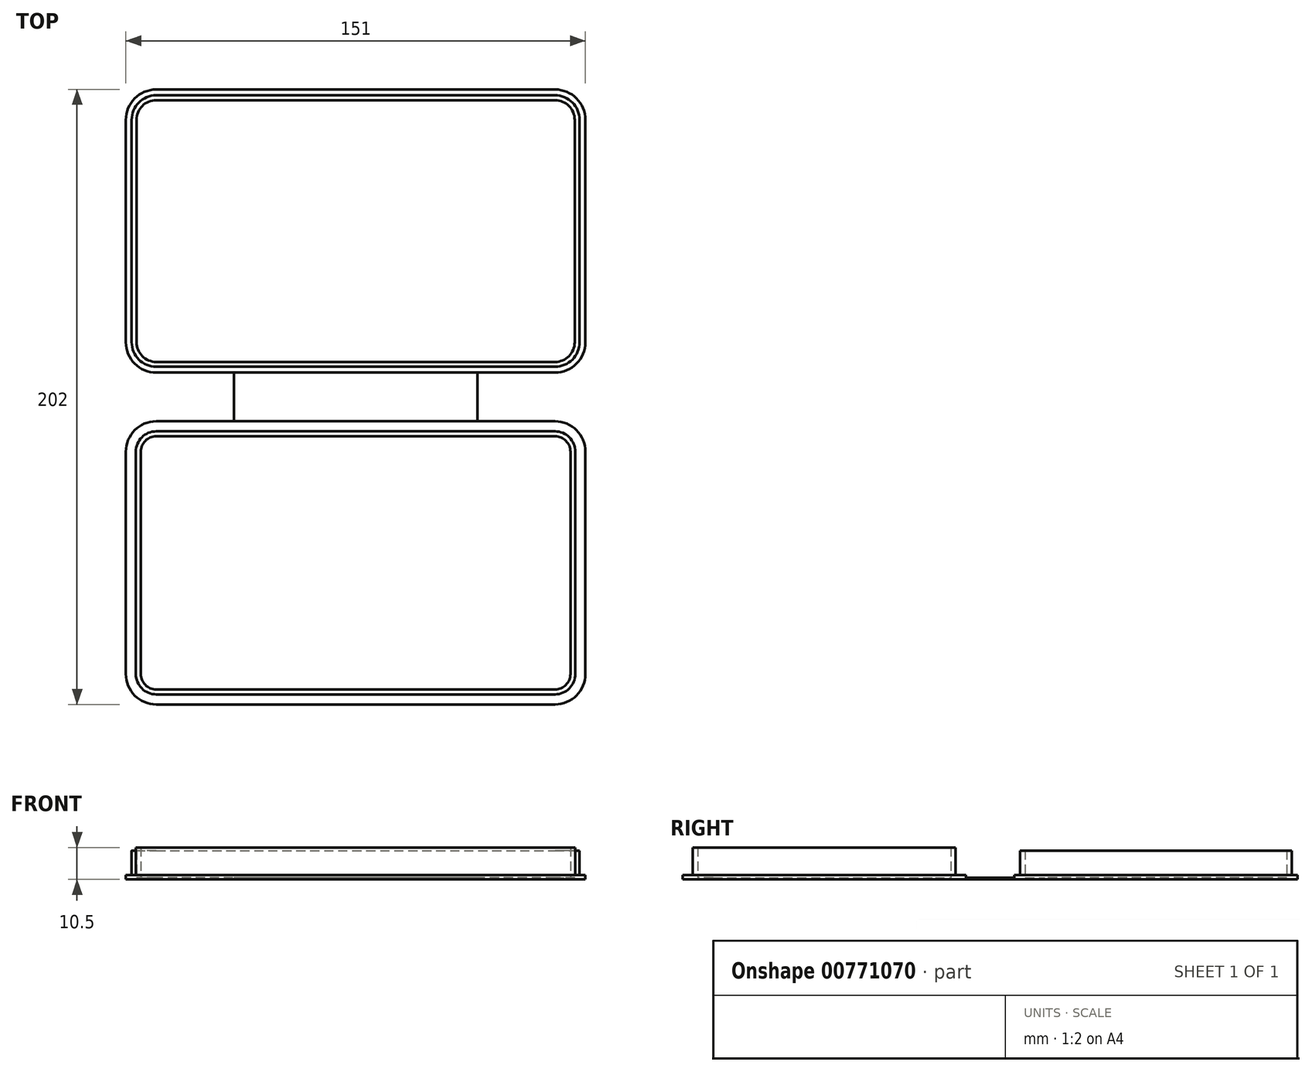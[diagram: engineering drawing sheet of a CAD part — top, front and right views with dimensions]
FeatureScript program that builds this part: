
annotation { "Feature Type Name" : "Feature", "Feature Type Description" : "" }
export const myFeature = defineFeature(function(context is Context, id is Id, definition is map)
    precondition{}
    {
        {
            var Q0;
            Q0=qCreatedBy(makeId("Top.planeOp"),FACE);
            var sketch = newSketch(context, id + "F0", { "sketchPlane" : qUnion([Q0])});
            skLineSegment(sketch, "E0.bottom", {"start": v(-40, 0) * mm, "end": v(40, 0) * mm});
            skLineSegment(sketch, "E0.left", {"start": v(-40, 0) * mm, "end": v(-40, -8) * mm});
            skLineSegment(sketch, "E0.right", {"start": v(40, 0) * mm, "end": v(40, -8) * mm});
            skLineSegment(sketch, "E1.bottom", {"start": v(-75.5, -8) * mm, "end": v(-40, -8) * mm});
            skLineSegment(sketch, "E1.top", {"start": v(-75.5, -101) * mm, "end": v(75.5, -101) * mm});
            skLineSegment(sketch, "E1.left", {"start": v(-75.5, -8) * mm, "end": v(-75.5, -101) * mm});
            skLineSegment(sketch, "E1.right", {"start": v(75.5, -8) * mm, "end": v(75.5, -101) * mm});
            skLineSegment(sketch, "E2.trimOffspring", {"start": v(40, -8) * mm, "end": v(75.5, -8) * mm});
            skLineSegment(sketch, "E3.bottom", {"start": v(71.5, -12) * mm, "end": v(-71.5, -12) * mm, "construction": true});
            skLineSegment(sketch, "E3.top", {"start": v(71.5, -97) * mm, "end": v(-71.5, -97) * mm, "construction": true});
            skLineSegment(sketch, "E3.left", {"start": v(71.5, -12) * mm, "end": v(71.5, -97) * mm, "construction": true});
            skLineSegment(sketch, "E3.right", {"start": v(-71.5, -12) * mm, "end": v(-71.5, -97) * mm, "construction": true});
            skPoint(sketch, "E3.middle", {"position": v(0, -54.5) * mm});
            skLineSegment(sketch, "E4", {"start": v(0, -12) * mm, "end": v(0, 0) * mm, "construction": true});
            skLineSegment(sketch, "E5", {"start": v(71.5, -54.5) * mm, "end": v(75.5, -54.5) * mm, "construction": true});
            skPoint(sketch, "E5.endSnap0", {"position": v(75.5, -54.5) * mm});
            skSolve(sketch);
        }
        {
            var Q0;
            Q0 = qSketchRegion(id + "F0", true);
            extrude(context, id + "F1", {"entities" : qUnion([Q0]), "depth" : 1.5 * mm, "offsetDistance" : 25 * mm});
        }
        {
            var Q0;
            Q0=makeQuery(id+"F1.opExtrude","SWEPT_EDGE",EDGE,{"disambiguationData":[OSD([sQuery(id+"F0.wireOp",EDGE,"E1.bottom"),sQuery(id+"F0.wireOp",EDGE,"E1.left")])]});
            var Q1;
            Q1=makeQuery(id+"F1.opExtrude","SWEPT_EDGE",EDGE,{"disambiguationData":[OSD([sQuery(id+"F0.wireOp",EDGE,"E1.top"),sQuery(id+"F0.wireOp",EDGE,"E1.left")])]});
            var Q2;
            Q2=makeQuery(id+"F1.opExtrude","SWEPT_EDGE",EDGE,{"disambiguationData":[OSD([sQuery(id+"F0.wireOp",EDGE,"E1.top"),sQuery(id+"F0.wireOp",EDGE,"E1.right")])]});
            var Q3;
            Q3=makeQuery(id+"F1.opExtrude","SWEPT_EDGE",EDGE,{"disambiguationData":[OSD([sQuery(id+"F0.wireOp",EDGE,"E1.right"),sQuery(id+"F0.wireOp",EDGE,"E2.trimOffspring")])]});
            fillet(context, id + "F2", {"entities" : qUnion([Q0, Q1, Q2, Q3]), "radius" : 10 * mm, "tangentPropagation" : true, "allowEdgeOverflow" : false});
        }
        {
            var Q0;
            Q0=makeQuery(id+"F1.opExtrude","SWEPT_BODY",BODY,{"disambiguationData":[OSD([sQuery(id+"F0.wireOp",EDGE,"E0.bottom"),sQuery(id+"F0.wireOp",EDGE,"E0.left"),sQuery(id+"F0.wireOp",EDGE,"E0.right"),sQuery(id+"F0.wireOp",EDGE,"E1.bottom"),sQuery(id+"F0.wireOp",EDGE,"E1.top"),sQuery(id+"F0.wireOp",EDGE,"E1.left"),sQuery(id+"F0.wireOp",EDGE,"E1.right"),sQuery(id+"F0.wireOp",EDGE,"E2.trimOffspring")])]});
            var Q1;
            Q1=makeQuery(id+"F1.opExtrude","SWEPT_FACE",FACE,{"disambiguationData":[OSD([sQuery(id+"F0.wireOp",EDGE,"E0.bottom")])]});
            mirror(context, id + "F3", {"operationType" : NewBodyOperationType.ADD, "entities" : qUnion([Q0]), "mirrorPlane" : qUnion([Q1])});
        }
        {
            var Q0;
            {var subQ0=makeQuery(id+"F1.opExtrude","CAP_FACE",FACE,{"disambiguationData":[OSD([sQuery(id+"F0.wireOp",EDGE,"E0.bottom"),sQuery(id+"F0.wireOp",EDGE,"E0.left"),sQuery(id+"F0.wireOp",EDGE,"E0.right"),sQuery(id+"F0.wireOp",EDGE,"E1.bottom"),sQuery(id+"F0.wireOp",EDGE,"E1.top"),sQuery(id+"F0.wireOp",EDGE,"E1.left"),sQuery(id+"F0.wireOp",EDGE,"E1.right"),sQuery(id+"F0.wireOp",EDGE,"E2.trimOffspring")])],"isStart":false});Q0=makeQuery(id+"F3.boolean.opBoolean","MERGE",FACE,{"derivedFrom":[subQ0,makeQuery(id+"F3.opPattern","COPY",FACE,{"derivedFrom":subQ0,"instanceName":"1"})]});}
            var sketch = newSketch(context, id + "F4", { "sketchPlane" : qUnion([Q0])});
            skLineSegment(sketch, "E6", {"start": v(-40, 8) * mm, "end": v(40, 8) * mm});
            skLineSegment(sketch, "E7", {"start": v(40, -8) * mm, "end": v(-40, -8) * mm});
            skSolve(sketch);
        }
        {
            var Q0;
            Q0=makeQuery(id+"F4.imprint","IMPRINT",FACE,{"disambiguationData":[TD([[makeQuery(id+"F4.imprint","IMPRINT",EDGE,{"derivedFrom":sQuery(id+"F4.wireOp",EDGE,"E7")}),1.0]])]});
            var sketch = newSketch(context, id + "F5", { "sketchPlane" : qUnion([Q0])});
            skLineSegment(sketch, "E8.0", {"start": v(40, -11.3) * mm, "end": v(65.5, -11.3) * mm});
            skArc(sketch, "E8.1", {"start": v(72.2, -18) * mm, "mid": v(70.24, -13.26) * mm, "end": v(65.5, -11.3) * mm});
            skLineSegment(sketch, "E8.2", {"start": v(40, -11.3) * mm, "end": v(-40, -11.3) * mm});
            skLineSegment(sketch, "E8.3", {"start": v(72.2, -18) * mm, "end": v(72.2, -91) * mm});
            skArc(sketch, "E8.4", {"start": v(65.5, -97.7) * mm, "mid": v(70.24, -95.74) * mm, "end": v(72.2, -91) * mm});
            skLineSegment(sketch, "E8.5", {"start": v(-65.5, -97.7) * mm, "end": v(65.5, -97.7) * mm});
            skLineSegment(sketch, "E8.6", {"start": v(-65.5, -11.3) * mm, "end": v(-40, -11.3) * mm});
            skArc(sketch, "E8.7", {"start": v(-65.5, -11.3) * mm, "mid": v(-70.24, -13.26) * mm, "end": v(-72.2, -18) * mm});
            skLineSegment(sketch, "E8.8", {"start": v(-72.2, -18) * mm, "end": v(-72.2, -91) * mm});
            skArc(sketch, "E8.9", {"start": v(-72.2, -91) * mm, "mid": v(-70.24, -95.74) * mm, "end": v(-65.5, -97.7) * mm});
            skArc(sketch, "E9.0", {"start": v(-72, 91) * mm, "mid": v(-70.1, 95.6) * mm, "end": v(-65.5, 97.5) * mm});
            skLineSegment(sketch, "E9.1", {"start": v(-72, 18) * mm, "end": v(-72, 91) * mm});
            skLineSegment(sketch, "E9.2", {"start": v(-65.5, 97.5) * mm, "end": v(65.5, 97.5) * mm});
            skArc(sketch, "E9.3", {"start": v(-65.5, 11.5) * mm, "mid": v(-70.1, 13.4) * mm, "end": v(-72, 18) * mm});
            skLineSegment(sketch, "E9.4", {"start": v(-65.5, 11.5) * mm, "end": v(-40, 11.5) * mm});
            skLineSegment(sketch, "E9.5", {"start": v(-40, 11.5) * mm, "end": v(40, 11.5) * mm});
            skArc(sketch, "E9.6", {"start": v(65.5, 97.5) * mm, "mid": v(70.1, 95.6) * mm, "end": v(72, 91) * mm});
            skLineSegment(sketch, "E9.7", {"start": v(72, 18) * mm, "end": v(72, 91) * mm});
            skArc(sketch, "E9.8", {"start": v(72, 18) * mm, "mid": v(70.1, 13.4) * mm, "end": v(65.5, 11.5) * mm});
            skLineSegment(sketch, "E9.9", {"start": v(40, 11.5) * mm, "end": v(65.5, 11.5) * mm});
            skLineSegment(sketch, "E10.0", {"start": v(-70.6, -18) * mm, "end": v(-70.6, -91) * mm});
            skArc(sketch, "E10.1", {"start": v(-65.5, -12.9) * mm, "mid": v(-69.1, -14.4) * mm, "end": v(-70.6, -18) * mm});
            skArc(sketch, "E10.2", {"start": v(-70.6, -91) * mm, "mid": v(-69.1, -94.6) * mm, "end": v(-65.5, -96.1) * mm});
            skLineSegment(sketch, "E10.3", {"start": v(-65.5, -12.9) * mm, "end": v(-40, -12.9) * mm});
            skLineSegment(sketch, "E10.4", {"start": v(40, -12.9) * mm, "end": v(-40, -12.9) * mm});
            skLineSegment(sketch, "E10.5", {"start": v(40, -12.9) * mm, "end": v(65.5, -12.9) * mm});
            skLineSegment(sketch, "E10.6", {"start": v(-65.5, -96.1) * mm, "end": v(65.5, -96.1) * mm});
            skArc(sketch, "E10.7", {"start": v(65.5, -96.1) * mm, "mid": v(69.1, -94.6) * mm, "end": v(70.6, -91) * mm});
            skLineSegment(sketch, "E10.8", {"start": v(70.6, -18) * mm, "end": v(70.6, -91) * mm});
            skArc(sketch, "E10.9", {"start": v(70.6, -18) * mm, "mid": v(69.1, -14.4) * mm, "end": v(65.5, -12.9) * mm});
            skArc(sketch, "E11.0", {"start": v(-65.5, 9.9) * mm, "mid": v(-71.23, 12.27) * mm, "end": v(-73.6, 18) * mm});
            skLineSegment(sketch, "E11.1", {"start": v(-65.5, 9.9) * mm, "end": v(-40, 9.9) * mm});
            skLineSegment(sketch, "E11.2", {"start": v(-73.6, 18) * mm, "end": v(-73.6, 91) * mm});
            skLineSegment(sketch, "E11.3", {"start": v(-40, 9.9) * mm, "end": v(40, 9.9) * mm});
            skLineSegment(sketch, "E11.4", {"start": v(40, 9.9) * mm, "end": v(65.5, 9.9) * mm});
            skArc(sketch, "E11.5", {"start": v(73.6, 18) * mm, "mid": v(71.23, 12.27) * mm, "end": v(65.5, 9.9) * mm});
            skArc(sketch, "E11.6", {"start": v(-73.6, 91) * mm, "mid": v(-71.23, 96.73) * mm, "end": v(-65.5, 99.1) * mm});
            skLineSegment(sketch, "E11.7", {"start": v(-65.5, 99.1) * mm, "end": v(65.5, 99.1) * mm});
            skArc(sketch, "E11.8", {"start": v(65.5, 99.1) * mm, "mid": v(71.23, 96.73) * mm, "end": v(73.6, 91) * mm});
            skLineSegment(sketch, "E11.9", {"start": v(73.6, 18) * mm, "end": v(73.6, 91) * mm});
            skSolve(sketch);
        }
        {
            var Q0;
            Q0 = qSketchRegion(id + "F5", true);
            extrude(context, id + "F6", {"entities" : qUnion([Q0]), "operationType" : NewBodyOperationType.ADD, "depth" : 8 * mm, "offsetDistance" : 25 * mm});
        }
        {
            var Q0;
            Q0=makeQuery(id+"F6.opExtrude","CAP_FACE",FACE,{"disambiguationData":[OSD([sQuery(id+"F5.wireOp",EDGE,"E8.0"),sQuery(id+"F5.wireOp",EDGE,"E8.1"),sQuery(id+"F5.wireOp",EDGE,"E8.2"),sQuery(id+"F5.wireOp",EDGE,"E8.3"),sQuery(id+"F5.wireOp",EDGE,"E8.4"),sQuery(id+"F5.wireOp",EDGE,"E8.5"),sQuery(id+"F5.wireOp",EDGE,"E8.6"),sQuery(id+"F5.wireOp",EDGE,"E8.7"),sQuery(id+"F5.wireOp",EDGE,"E8.8"),sQuery(id+"F5.wireOp",EDGE,"E8.9"),sQuery(id+"F5.wireOp",EDGE,"E10.0"),sQuery(id+"F5.wireOp",EDGE,"E10.1"),sQuery(id+"F5.wireOp",EDGE,"E10.2"),sQuery(id+"F5.wireOp",EDGE,"E10.3"),sQuery(id+"F5.wireOp",EDGE,"E10.4"),sQuery(id+"F5.wireOp",EDGE,"E10.5"),sQuery(id+"F5.wireOp",EDGE,"E10.6"),sQuery(id+"F5.wireOp",EDGE,"E10.7"),sQuery(id+"F5.wireOp",EDGE,"E10.8"),sQuery(id+"F5.wireOp",EDGE,"E10.9")])],"isStart":false});
            extrude(context, id + "F7", {"entities" : qUnion([Q0]), "operationType" : NewBodyOperationType.ADD, "depth" : 1 * mm, "offsetDistance" : 25 * mm});
        }
        {
            var Q0;
            Q0=makeQuery(id+"F4.imprint","IMPRINT",FACE,{"disambiguationData":[TD([[makeQuery(id+"F4.imprint","IMPRINT",EDGE,{"derivedFrom":sQuery(id+"F4.wireOp",EDGE,"E6")}),1.0]])]});
            var sketch = newSketch(context, id + "F8", { "sketchPlane" : qUnion([Q0])});
            skLineSegment(sketch, "E12.0", {"start": v(-65.5, 97.5) * mm, "end": v(65.5, 97.5) * mm});
            skArc(sketch, "E12.1", {"start": v(-72, 91) * mm, "mid": v(-70.1, 95.6) * mm, "end": v(-65.5, 97.5) * mm});
            skLineSegment(sketch, "E12.2", {"start": v(-72, 18) * mm, "end": v(-72, 91) * mm});
            skArc(sketch, "E12.3", {"start": v(-65.5, 11.5) * mm, "mid": v(-70.1, 13.4) * mm, "end": v(-72, 18) * mm});
            skLineSegment(sketch, "E12.4", {"start": v(-65.5, 11.5) * mm, "end": v(65.5, 11.5) * mm});
            skArc(sketch, "E12.5", {"start": v(72, 18) * mm, "mid": v(70.1, 13.4) * mm, "end": v(65.5, 11.5) * mm});
            skArc(sketch, "E12.6", {"start": v(65.5, 97.5) * mm, "mid": v(70.1, 95.6) * mm, "end": v(72, 91) * mm});
            skLineSegment(sketch, "E12.7", {"start": v(72, 18) * mm, "end": v(72, 91) * mm});
            skLineSegment(sketch, "E13.bottom", {"start": v(-40, 8) * mm, "end": v(40, 8) * mm});
            skLineSegment(sketch, "E13.top", {"start": v(-40, -8) * mm, "end": v(40, -8) * mm});
            skLineSegment(sketch, "E13.left", {"start": v(-40, 8) * mm, "end": v(-40, -8) * mm});
            skLineSegment(sketch, "E13.right", {"start": v(40, 8) * mm, "end": v(40, -8) * mm});
            skPoint(sketch, "E13.middle", {"position": v(0, 0) * mm});
            skArc(sketch, "E14.0", {"start": v(70.6, -18) * mm, "mid": v(69.1, -14.4) * mm, "end": v(65.5, -12.9) * mm});
            skLineSegment(sketch, "E14.1", {"start": v(-65.5, -12.9) * mm, "end": v(65.5, -12.9) * mm});
            skLineSegment(sketch, "E14.2", {"start": v(70.6, -18) * mm, "end": v(70.6, -91) * mm});
            skArc(sketch, "E14.3", {"start": v(-65.5, -12.9) * mm, "mid": v(-69.1, -14.4) * mm, "end": v(-70.6, -18) * mm});
            skLineSegment(sketch, "E14.4", {"start": v(-70.6, -18) * mm, "end": v(-70.6, -91) * mm});
            skArc(sketch, "E14.5", {"start": v(-70.6, -91) * mm, "mid": v(-69.1, -94.6) * mm, "end": v(-65.5, -96.1) * mm});
            skLineSegment(sketch, "E14.6", {"start": v(-65.5, -96.1) * mm, "end": v(65.5, -96.1) * mm});
            skArc(sketch, "E14.7", {"start": v(65.5, -96.1) * mm, "mid": v(69.1, -94.6) * mm, "end": v(70.6, -91) * mm});
            skSolve(sketch);
        }
        {
            var Q0;
            Q0 = qSketchRegion(id + "F8", true);
            var Q1;
            {var subQ0=makeQuery(id+"F1.opExtrude","CAP_FACE",FACE,{"disambiguationData":[OSD([sQuery(id+"F0.wireOp",EDGE,"E0.bottom"),sQuery(id+"F0.wireOp",EDGE,"E0.left"),sQuery(id+"F0.wireOp",EDGE,"E0.right"),sQuery(id+"F0.wireOp",EDGE,"E1.bottom"),sQuery(id+"F0.wireOp",EDGE,"E1.top"),sQuery(id+"F0.wireOp",EDGE,"E1.left"),sQuery(id+"F0.wireOp",EDGE,"E1.right"),sQuery(id+"F0.wireOp",EDGE,"E2.trimOffspring")])],"isStart":true});Q1=makeQuery(id+"F3.boolean.opBoolean","MERGE",FACE,{"derivedFrom":[subQ0,makeQuery(id+"F3.opPattern","COPY",FACE,{"derivedFrom":subQ0,"instanceName":"1"})]});}
            extrude(context, id + "F9", {"entities" : qUnion([Q0]), "operationType" : NewBodyOperationType.REMOVE, "endBound" : BoundingType.UP_TO_SURFACE, "oppositeDirection" : true, "depth" : 25 * mm, "endBoundEntityFace" : qUnion([Q1]), "hasOffset" : true, "offsetDistance" : .5 * mm});
        }
    });
